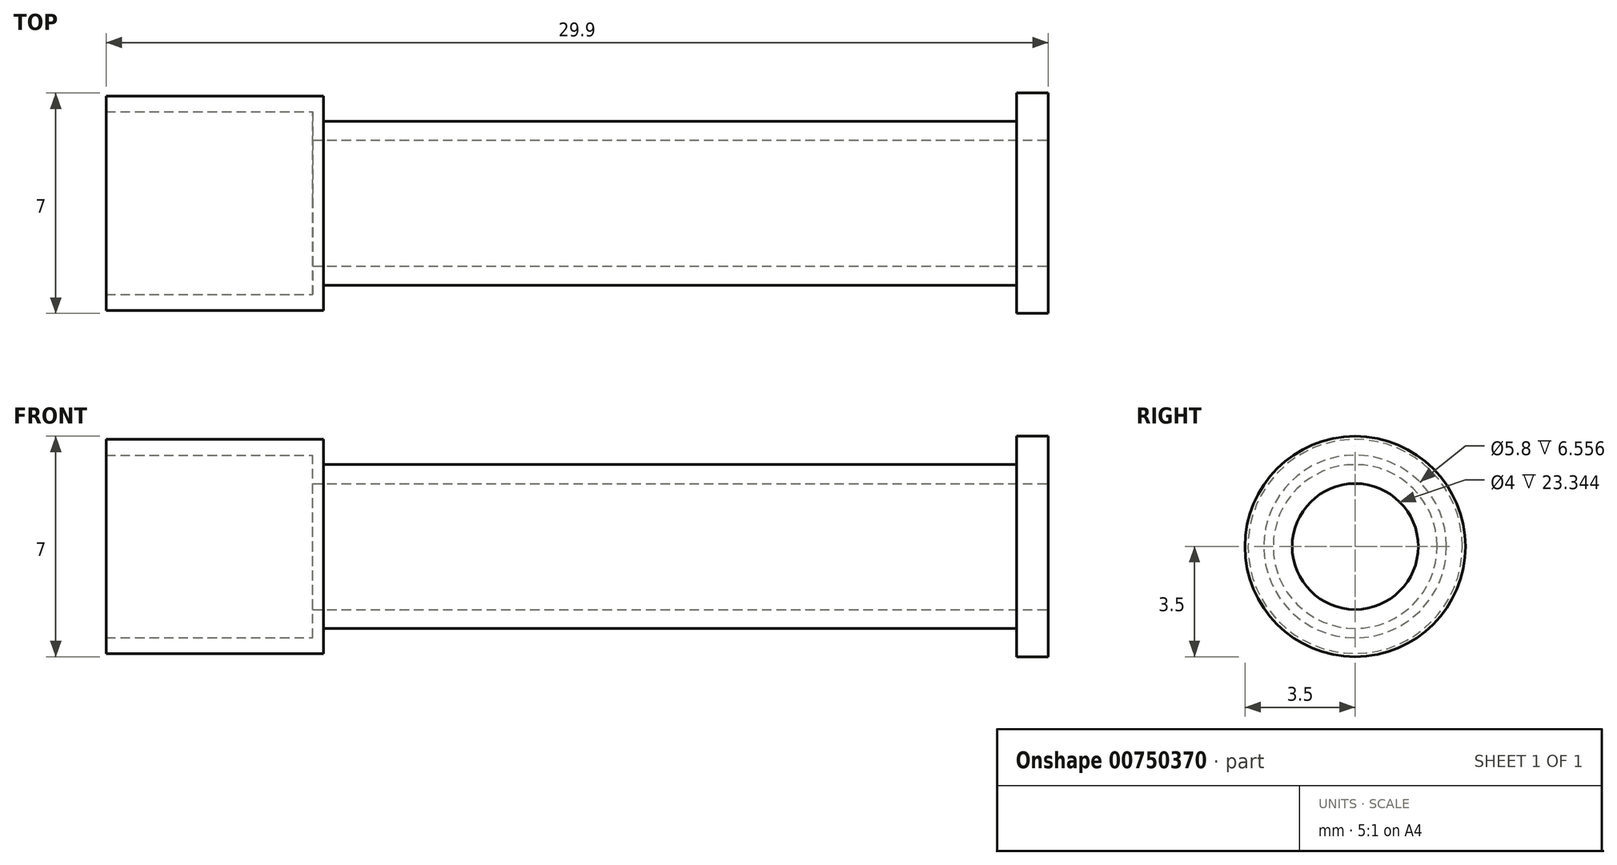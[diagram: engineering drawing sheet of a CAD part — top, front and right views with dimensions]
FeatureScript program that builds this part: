
annotation { "Feature Type Name" : "Feature", "Feature Type Description" : "" }
export const myFeature = defineFeature(function(context is Context, id is Id, definition is map)
    precondition{}
    {
        {
            var Q0;
            Q0=qCreatedBy(makeId("Front.planeOp"),FACE);
            var sketch = newSketch(context, id + "F0", { "sketchPlane" : qUnion([Q0])});
            skLineSegment(sketch, "E0", {"start": v(-12.36, 0) * mm, "end": v(17.73, 0) * mm});
            skLineSegment(sketch, "E1", {"start": v(17.73, 0) * mm, "end": v(17.73, 2.6) * mm});
            skLineSegment(sketch, "E2", {"start": v(17.73, 2.6) * mm, "end": v(-4.27, 2.6) * mm});
            skLineSegment(sketch, "E3", {"start": v(-4.27, 2.6) * mm, "end": v(-4.27, 3.4) * mm});
            skLineSegment(sketch, "E4", {"start": v(-4.27, 3.4) * mm, "end": v(-11.17, 3.4) * mm});
            skLineSegment(sketch, "E5", {"start": v(-11.17, 3.4) * mm, "end": v(-11.17, 0) * mm});
            skLineSegment(sketch, "E6", {"start": v(17.73, 2.6) * mm, "end": v(17.73, 3.5) * mm});
            skLineSegment(sketch, "E7", {"start": v(17.73, 3.5) * mm, "end": v(18.73, 3.5) * mm});
            skLineSegment(sketch, "E8", {"start": v(18.73, 3.5) * mm, "end": v(18.73, 0) * mm});
            skLineSegment(sketch, "E9", {"start": v(18.73, 0) * mm, "end": v(17.73, 0) * mm});
            skSolve(sketch);
        }
        {
            var Q0;
            Q0 = qSketchRegion(id + "F0", true);
            var Q1;
            Q1=sQuery(id+"F0.wireOp",EDGE,"E0");
            revolve(context, id + "F1", {"surfaceOperationType" : NewSurfaceOperationType.NEW, "entities" : qUnion([Q0]), "axis" : qUnion([Q1]), "revolveType" : RevolveType.FULL});
        }
        {
            var Q0;
            Q0=qCreatedBy(makeId("Front.planeOp"),FACE);
            var sketch = newSketch(context, id + "F2", { "sketchPlane" : qUnion([Q0])});
            skLineSegment(sketch, "E10", {"start": v(-13.65, 0) * mm, "end": v(20.5, 0) * mm});
            skLineSegment(sketch, "E11", {"start": v(20.5, 0) * mm, "end": v(20.5, 2) * mm});
            skLineSegment(sketch, "E12", {"start": v(20.5, 2) * mm, "end": v(-4.62, 2) * mm});
            skLineSegment(sketch, "E13", {"start": v(-4.62, 2) * mm, "end": v(-4.62, 2.9) * mm});
            skLineSegment(sketch, "E14", {"start": v(-4.62, 2.9) * mm, "end": v(-12.32, 2.9) * mm});
            skLineSegment(sketch, "E15", {"start": v(-12.32, 2.9) * mm, "end": v(-12.32, 0) * mm});
            skSolve(sketch);
        }
        {
            var Q0;
            Q0 = qSketchRegion(id + "F2", true);
            var Q1;
            Q1=sQuery(id+"F2.wireOp",EDGE,"E10");
            revolve(context, id + "F3", {"operationType" : NewBodyOperationType.REMOVE, "surfaceOperationType" : NewSurfaceOperationType.NEW, "entities" : qUnion([Q0]), "axis" : qUnion([Q1]), "revolveType" : RevolveType.FULL, "oppositeDirection" : true});
        }
    });
